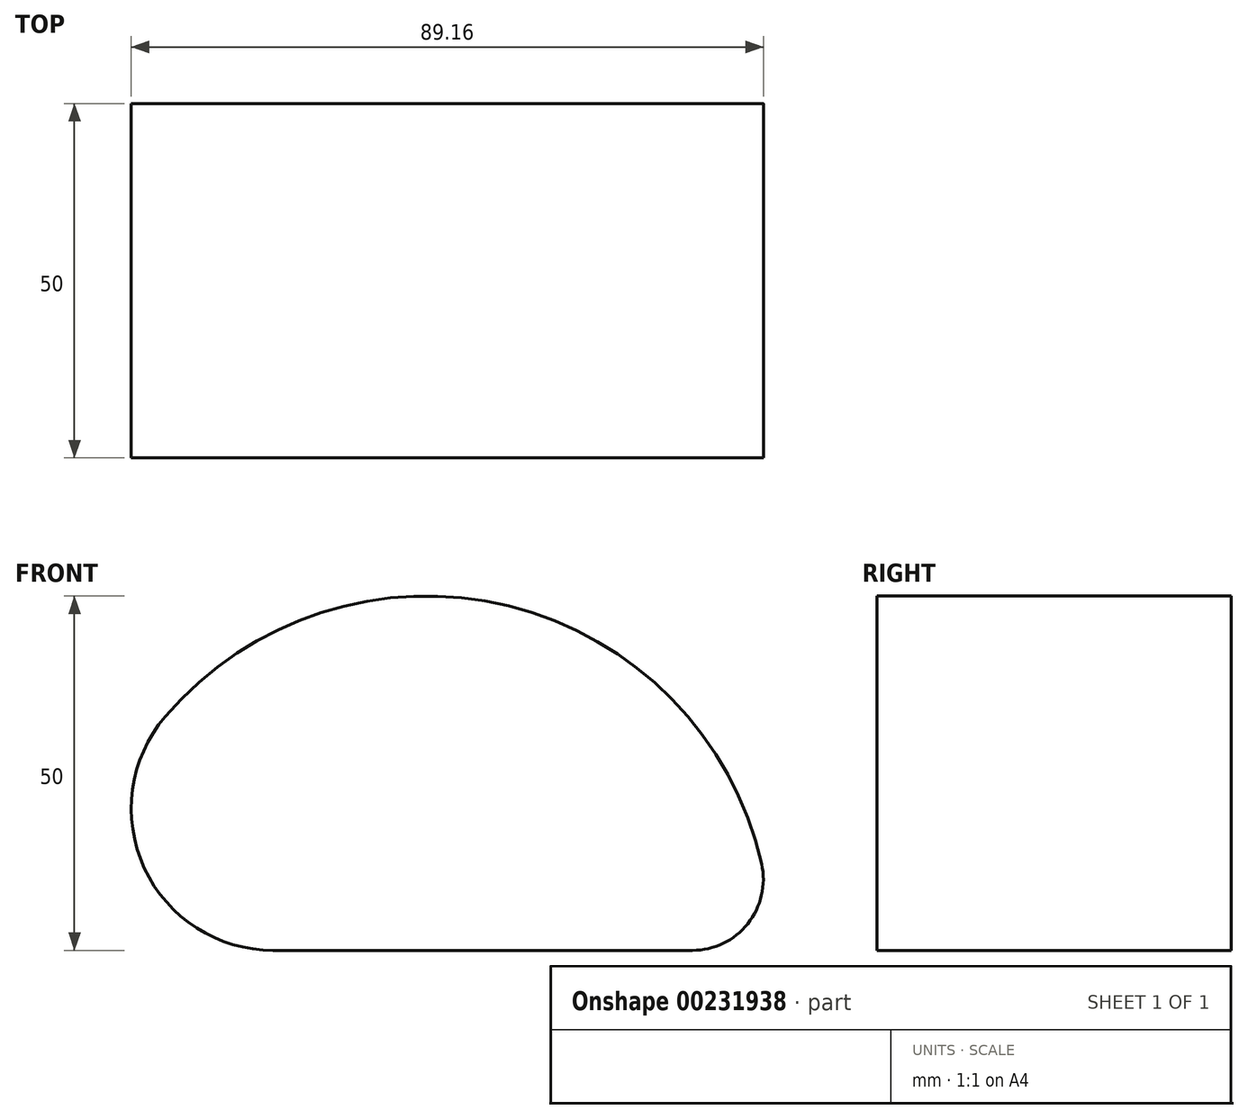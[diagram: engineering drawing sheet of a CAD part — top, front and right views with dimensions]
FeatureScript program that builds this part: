
annotation { "Feature Type Name" : "Feature", "Feature Type Description" : "" }
export const myFeature = defineFeature(function(context is Context, id is Id, definition is map)
    precondition{}
    {
        {
            var Q0;
            Q0=qCreatedBy(makeId("Front.planeOp"),FACE);
            var sketch = newSketch(context, id + "F0", { "sketchPlane" : qUnion([Q0])});
            skLineSegment(sketch, "E0", {"start": v(0, 0) * mm, "end": v(-59.16, 0) * mm});
            skArc(sketch, "E1", {"start": v(-59.16, 0) * mm, "mid": v(-77.32, 11.61) * mm, "end": v(-74.39, 32.97) * mm});
            skArc(sketch, "E2", {"start": v(-74.39, 32.97) * mm, "mid": v(-25.9, 48.59) * mm, "end": v(9.76, 12.2) * mm});
            skArc(sketch, "E3", {"start": v(9.76, 12.2) * mm, "mid": v(7.8, 3.75) * mm, "end": v(0, 0) * mm});
            skSolve(sketch);
        }
        {
            var Q0;
            Q0=makeQuery(id+"F0.imprint","IMPRINT",FACE,{"disambiguationData":[TD([[makeQuery(id+"F0.imprint","IMPRINT",EDGE,{"derivedFrom":sQuery(id+"F0.wireOp",EDGE,"E0")}),-1.0]])]});
            extrude(context, id + "F1", {"entities" : qUnion([Q0]), "endBound" : BoundingType.SYMMETRIC, "depth" : 50 * mm});
        }
    });
